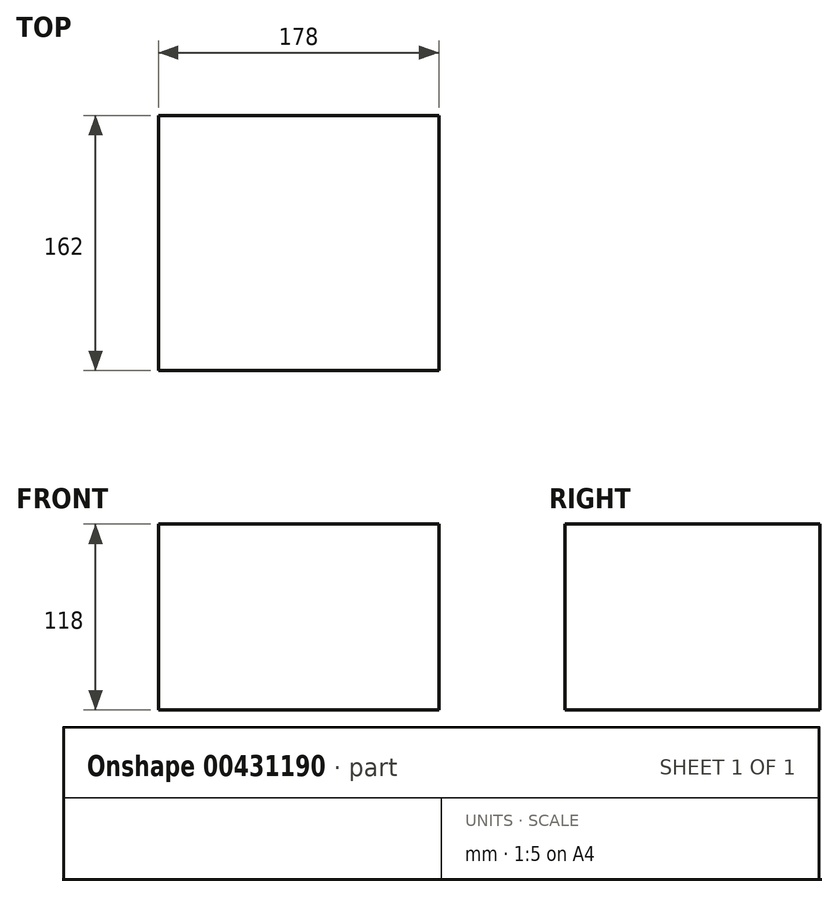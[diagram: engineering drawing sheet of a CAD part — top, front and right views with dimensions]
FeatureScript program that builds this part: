
annotation { "Feature Type Name" : "Feature", "Feature Type Description" : "" }
export const myFeature = defineFeature(function(context is Context, id is Id, definition is map)
    precondition{}
    {
        {
            var Q0;
            Q0=qCreatedBy(makeId("Top.planeOp"),FACE);
            var sketch = newSketch(context, id + "F0", { "sketchPlane" : qUnion([Q0])});
            skLineSegment(sketch, "E0.bottom", {"start": v(0, 0) * mm, "end": v(178, 0) * mm});
            skLineSegment(sketch, "E0.top", {"start": v(0, -162) * mm, "end": v(178, -162) * mm});
            skLineSegment(sketch, "E0.left", {"start": v(0, 0) * mm, "end": v(0, -162) * mm});
            skLineSegment(sketch, "E0.right", {"start": v(178, 0) * mm, "end": v(178, -162) * mm});
            skSolve(sketch);
        }
        {
            var Q0;
            Q0=makeQuery(id+"F0.imprint","IMPRINT",FACE,{"disambiguationData":[TD([[makeQuery(id+"F0.imprint","IMPRINT",EDGE,{"derivedFrom":sQuery(id+"F0.wireOp",EDGE,"E0.bottom")}),-1.0]])]});
            extrude(context, id + "F1", {"entities" : qUnion([Q0]), "depth" : 118 * mm});
        }
    });
